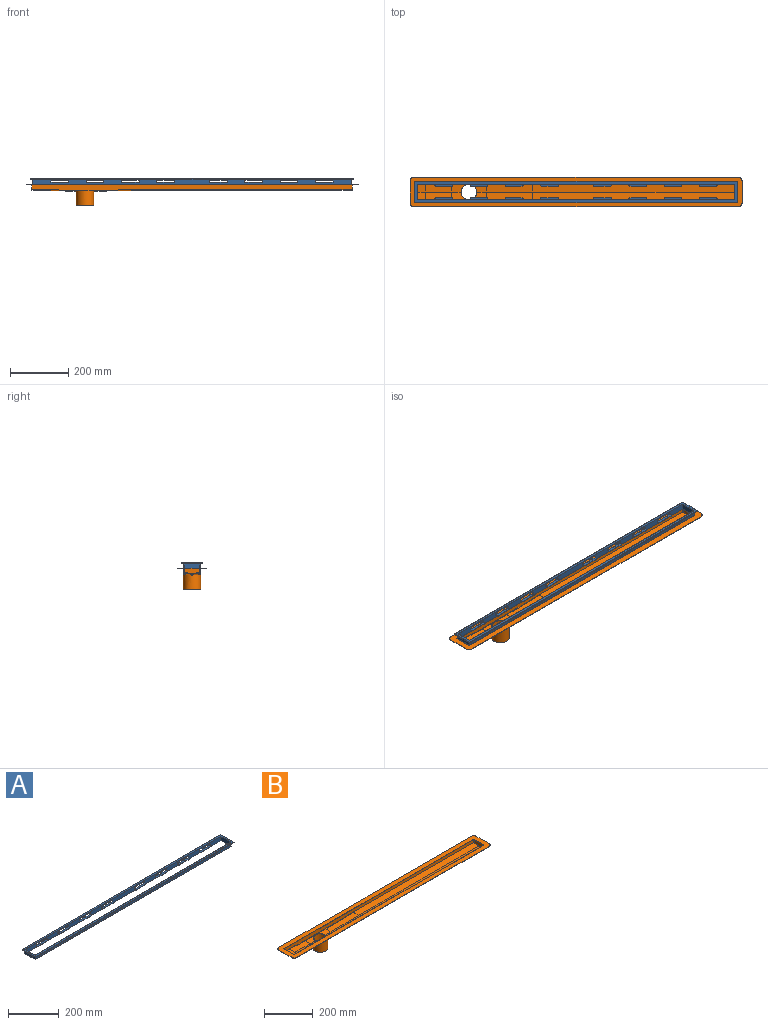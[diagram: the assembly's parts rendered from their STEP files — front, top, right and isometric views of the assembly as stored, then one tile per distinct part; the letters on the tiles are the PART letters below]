
ASSEMBLY  parts=2 mates=1
PART A: 212 faces, bbox 1112.8x73x20.6 mm
  f0: plane 1093.79x20.64mm, normal (0,1,0), area 17992.5mm2, adj f6,f7,f9,f12,f13,f17,f19,f23
  f1: plane 1096.96x19.05mm, normal (0,-1,0), area 17088.3mm2, adj f2,f6,f10,f18,f25,f32,f39,f40
  f2: plane 1109.66x69.85mm, normal (0,0,-1), area 14818.5mm2, adj f1,f5,f10,f11,f61,f63,f114,f115
  f3: plane 1112.84x3.18mm, normal (0,-1,0), area 3533.3mm2, adj f4,f7,f8,f112
  f4: plane 1112.84x73.03mm, normal (0,0,-1), area 3755mm2, adj f3,f5,f8,f11,f62,f63,f112,f115
  f5: plane 1109.66x1.59mm, normal (0,1,0), area 1761.6mm2, adj f2,f4,f11,f115
  f6: plane 1096.96x57.15mm, normal (0,0,-1), area 3654.2mm2, adj f0,f1,f9,f10,f60,f61,f113,f114
  f7: plane 1112.84x73.03mm, normal (0,0,1), area 22227.8mm2, adj f0,f3,f8,f9,f60,f62,f112,f113
  f8: plane 73.03x3.18mm, normal (1,0,0), area 231.9mm2, adj f3,f4,f7,f62
  f9: plane 53.98x20.64mm, normal (-1,0,0), area 1113.9mm2, adj f0,f6,f7,f60
  f10: plane 57.15x19.05mm, normal (1,0,0), area 1088.7mm2, adj f1,f2,f6,f61
  f11: plane 69.85x1.59mm, normal (-1,0,0), area 110.9mm2, adj f2,f4,f5,f63
  f12: plane 4.13x1.59mm, normal (-1,0,0), area 6.6mm2, adj f0,f16,f17,f18
  f13: plane 4.13x1.59mm, normal (1,0,0), area 6.6mm2, adj f0,f14,f17,f18
  f14: cylinder r=3.81mm len=3.81mm, axis (0,0,1), area 9.5mm2, adj f13,f15,f17,f18
  f15: plane 53.15x1.59mm, normal (0,1,0), area 84.4mm2, adj f14,f16,f17,f18
  f16: cylinder r=3.81mm len=3.81mm, axis (0,0,1), area 9.5mm2, adj f12,f15,f17,f18
  f17: plane 60.77x7.94mm, normal (0,0,-1), area 476.1mm2, adj f0,f12,f13,f14,f15,f16
  f18: plane 60.77x9.53mm, normal (0,0,1), area 572.6mm2, adj f1,f12,f13,f14,f15,f16,f40,f44
  f19: plane 4.13x1.59mm, normal (1,0,0), area 6.6mm2, adj f0,f20,f24,f25
  f20: cylinder r=3.81mm len=3.81mm, axis (0,0,1), area 9.5mm2, adj f19,f21,f24,f25
  f21: plane 53.15x1.59mm, normal (0,1,0), area 84.4mm2, adj f20,f22,f24,f25
  f22: cylinder r=3.81mm len=3.81mm, axis (0,0,1), area 9.5mm2, adj f21,f23,f24,f25
  f23: plane 4.13x1.59mm, normal (-1,0,0), area 6.6mm2, adj f0,f22,f24,f25
  f24: plane 60.77x7.94mm, normal (0,0,-1), area 476.1mm2, adj f0,f19,f20,f21,f22,f23
  f25: plane 60.77x9.53mm, normal (0,0,1), area 572.6mm2, adj f1,f19,f20,f21,f22,f23,f45,f49
  f26: plane 4.13x1.59mm, normal (1,0,0), area 6.6mm2, adj f0,f27,f31,f32
  f27: cylinder r=3.81mm len=3.81mm, axis (0,0,1), area 9.5mm2, adj f26,f28,f31,f32
  f28: plane 53.15x1.59mm, normal (0,1,0), area 84.4mm2, adj f27,f29,f31,f32
  f29: cylinder r=3.81mm len=3.81mm, axis (0,0,1), area 9.5mm2, adj f28,f30,f31,f32
  f30: plane 4.13x1.59mm, normal (-1,0,0), area 6.6mm2, adj f0,f29,f31,f32
  f31: plane 60.77x7.94mm, normal (0,0,-1), area 476.1mm2, adj f0,f26,f27,f28,f29,f30
  f32: plane 60.77x9.53mm, normal (0,0,1), area 572.6mm2, adj f1,f26,f27,f28,f29,f30,f50,f54
  f33: plane 4.13x1.59mm, normal (1,0,0), area 6.6mm2, adj f0,f34,f38,f39
  f34: cylinder r=3.81mm len=3.81mm, axis (0,0,1), area 9.5mm2, adj f33,f35,f38,f39
  f35: plane 53.15x1.59mm, normal (0,1,0), area 84.4mm2, adj f34,f36,f38,f39
  f36: cylinder r=3.81mm len=3.81mm, axis (0,0,1), area 9.5mm2, adj f35,f37,f38,f39
  f37: plane 4.13x1.59mm, normal (-1,0,0), area 6.6mm2, adj f0,f36,f38,f39
  f38: plane 60.77x7.94mm, normal (0,0,-1), area 476.1mm2, adj f0,f33,f34,f35,f36,f37
  f39: plane 60.77x9.53mm, normal (0,0,1), area 572.6mm2, adj f1,f33,f34,f35,f36,f37,f56,f57
  f40: plane 4.13x1.59mm, normal (1,0,0), area 6.6mm2, adj f0,f1,f18,f41
  f41: cylinder r=3.81mm len=3.81mm, axis (0,1,0), area 9.5mm2, adj f0,f1,f40,f42
  f42: plane 53.15x1.59mm, normal (0,0,-1), area 84.4mm2, adj f0,f1,f41,f43
  f43: cylinder r=3.81mm len=3.81mm, axis (0,1,0), area 9.5mm2, adj f0,f1,f42,f44
  f44: plane 4.13x1.59mm, normal (-1,0,0), area 6.6mm2, adj f0,f1,f18,f43
  f45: plane 4.13x1.59mm, normal (1,0,0), area 6.6mm2, adj f0,f1,f25,f46
  f46: cylinder r=3.81mm len=3.81mm, axis (0,1,0), area 9.5mm2, adj f0,f1,f45,f47
  f47: plane 53.15x1.59mm, normal (0,0,-1), area 84.4mm2, adj f0,f1,f46,f48
  f48: cylinder r=3.81mm len=3.81mm, axis (0,1,0), area 9.5mm2, adj f0,f1,f47,f49
  f49: plane 4.13x1.59mm, normal (-1,0,0), area 6.6mm2, adj f0,f1,f25,f48
  f50: plane 4.13x1.59mm, normal (1,0,0), area 6.6mm2, adj f0,f1,f32,f51
  f51: cylinder r=3.81mm len=3.81mm, axis (0,1,0), area 9.5mm2, adj f0,f1,f50,f52
  f52: plane 53.15x1.59mm, normal (0,0,-1), area 84.4mm2, adj f0,f1,f51,f53
  f53: cylinder r=3.81mm len=3.81mm, axis (0,1,0), area 9.5mm2, adj f0,f1,f52,f54
  f54: plane 4.13x1.59mm, normal (-1,0,0), area 6.6mm2, adj f0,f1,f32,f53
  f55: cylinder r=3.81mm len=3.81mm, axis (0,1,0), area 9.5mm2, adj f0,f1,f56,f59
  f56: plane 4.13x1.59mm, normal (-1,0,0), area 6.6mm2, adj f0,f1,f39,f55
  f57: plane 4.13x1.59mm, normal (1,0,0), area 6.6mm2, adj f0,f1,f39,f58
  f58: cylinder r=3.81mm len=3.81mm, axis (0,1,0), area 9.5mm2, adj f0,f1,f57,f59
  f59: plane 53.15x1.59mm, normal (0,0,-1), area 84.4mm2, adj f0,f1,f55,f58
  f60: plane 1093.79x20.64mm, normal (0,-1,0), area 17992.5mm2, adj f6,f7,f9,f64,f65,f69,f71,f75
  f61: plane 1096.96x19.05mm, normal (0,1,0), area 17088.3mm2, adj f2,f6,f10,f70,f77,f84,f91,f92
  f62: plane 1112.84x3.18mm, normal (0,1,0), area 3533.3mm2, adj f4,f7,f8,f112
  f63: plane 1109.66x1.59mm, normal (0,-1,0), area 1761.6mm2, adj f2,f4,f11,f115
  f64: plane 4.13x1.59mm, normal (-1,0,0), area 6.6mm2, adj f60,f68,f69,f70
  f65: plane 4.13x1.59mm, normal (1,0,0), area 6.6mm2, adj f60,f66,f69,f70
  f66: cylinder r=3.81mm len=3.81mm, axis (0,0,1), area 9.5mm2, adj f65,f67,f69,f70
  f67: plane 53.15x1.59mm, normal (0,-1,0), area 84.4mm2, adj f66,f68,f69,f70
  f68: cylinder r=3.81mm len=3.81mm, axis (0,0,1), area 9.5mm2, adj f64,f67,f69,f70
  f69: plane 60.77x7.94mm, normal (0,0,-1), area 476.1mm2, adj f60,f64,f65,f66,f67,f68
  f70: plane 60.77x9.53mm, normal (0,0,1), area 572.6mm2, adj f61,f64,f65,f66,f67,f68,f92,f96
  f71: plane 4.13x1.59mm, normal (1,0,0), area 6.6mm2, adj f60,f72,f76,f77
  f72: cylinder r=3.81mm len=3.81mm, axis (0,0,1), area 9.5mm2, adj f71,f73,f76,f77
  f73: plane 53.15x1.59mm, normal (0,-1,0), area 84.4mm2, adj f72,f74,f76,f77
  f74: cylinder r=3.81mm len=3.81mm, axis (0,0,1), area 9.5mm2, adj f73,f75,f76,f77
  f75: plane 4.13x1.59mm, normal (-1,0,0), area 6.6mm2, adj f60,f74,f76,f77
  f76: plane 60.77x7.94mm, normal (0,0,-1), area 476.1mm2, adj f60,f71,f72,f73,f74,f75
  f77: plane 60.77x9.53mm, normal (0,0,1), area 572.6mm2, adj f61,f71,f72,f73,f74,f75,f97,f101
  f78: plane 4.13x1.59mm, normal (1,0,0), area 6.6mm2, adj f60,f79,f83,f84
  f79: cylinder r=3.81mm len=3.81mm, axis (0,0,1), area 9.5mm2, adj f78,f80,f83,f84
  f80: plane 53.15x1.59mm, normal (0,-1,0), area 84.4mm2, adj f79,f81,f83,f84
  f81: cylinder r=3.81mm len=3.81mm, axis (0,0,1), area 9.5mm2, adj f80,f82,f83,f84
  f82: plane 4.13x1.59mm, normal (-1,0,0), area 6.6mm2, adj f60,f81,f83,f84
  f83: plane 60.77x7.94mm, normal (0,0,-1), area 476.1mm2, adj f60,f78,f79,f80,f81,f82
  f84: plane 60.77x9.53mm, normal (0,0,1), area 572.6mm2, adj f61,f78,f79,f80,f81,f82,f102,f106
  f85: plane 4.13x1.59mm, normal (1,0,0), area 6.6mm2, adj f60,f86,f90,f91
  f86: cylinder r=3.81mm len=3.81mm, axis (0,0,1), area 9.5mm2, adj f85,f87,f90,f91
  f87: plane 53.15x1.59mm, normal (0,-1,0), area 84.4mm2, adj f86,f88,f90,f91
  f88: cylinder r=3.81mm len=3.81mm, axis (0,0,1), area 9.5mm2, adj f87,f89,f90,f91
  f89: plane 4.13x1.59mm, normal (-1,0,0), area 6.6mm2, adj f60,f88,f90,f91
  f90: plane 60.77x7.94mm, normal (0,0,-1), area 476.1mm2, adj f60,f85,f86,f87,f88,f89
  f91: plane 60.77x9.53mm, normal (0,0,1), area 572.6mm2, adj f61,f85,f86,f87,f88,f89,f108,f109
  f92: plane 4.13x1.59mm, normal (1,0,0), area 6.6mm2, adj f60,f61,f70,f93
  f93: cylinder r=3.81mm len=3.81mm, axis (0,-1,0), area 9.5mm2, adj f60,f61,f92,f94
  f94: plane 53.15x1.59mm, normal (0,0,-1), area 84.4mm2, adj f60,f61,f93,f95
  f95: cylinder r=3.81mm len=3.81mm, axis (0,-1,0), area 9.5mm2, adj f60,f61,f94,f96
  f96: plane 4.13x1.59mm, normal (-1,0,0), area 6.6mm2, adj f60,f61,f70,f95
  f97: plane 4.13x1.59mm, normal (1,0,0), area 6.6mm2, adj f60,f61,f77,f98
  f98: cylinder r=3.81mm len=3.81mm, axis (0,-1,0), area 9.5mm2, adj f60,f61,f97,f99
  f99: plane 53.15x1.59mm, normal (0,0,-1), area 84.4mm2, adj f60,f61,f98,f100
  f100: cylinder r=3.81mm len=3.81mm, axis (0,-1,0), area 9.5mm2, adj f60,f61,f99,f101
  f101: plane 4.13x1.59mm, normal (-1,0,0), area 6.6mm2, adj f60,f61,f77,f100
  f102: plane 4.13x1.59mm, normal (1,0,0), area 6.6mm2, adj f60,f61,f84,f103
  f103: cylinder r=3.81mm len=3.81mm, axis (0,-1,0), area 9.5mm2, adj f60,f61,f102,f104
  f104: plane 53.15x1.59mm, normal (0,0,-1), area 84.4mm2, adj f60,f61,f103,f105
  f105: cylinder r=3.81mm len=3.81mm, axis (0,-1,0), area 9.5mm2, adj f60,f61,f104,f106
  f106: plane 4.13x1.59mm, normal (-1,0,0), area 6.6mm2, adj f60,f61,f84,f105
  f107: cylinder r=3.81mm len=3.81mm, axis (0,-1,0), area 9.5mm2, adj f60,f61,f108,f111
  f108: plane 4.13x1.59mm, normal (-1,0,0), area 6.6mm2, adj f60,f61,f91,f107
  f109: plane 4.13x1.59mm, normal (1,0,0), area 6.6mm2, adj f60,f61,f91,f110
  f110: cylinder r=3.81mm len=3.81mm, axis (0,-1,0), area 9.5mm2, adj f60,f61,f109,f111
  f111: plane 53.15x1.59mm, normal (0,0,-1), area 84.4mm2, adj f60,f61,f107,f110
  f112: plane 73.03x3.18mm, normal (-1,0,0), area 231.9mm2, adj f3,f4,f7,f62
  f113: plane 53.98x20.64mm, normal (1,0,0), area 1113.9mm2, adj f0,f6,f7,f60
  f114: plane 57.15x19.05mm, normal (-1,0,0), area 1088.7mm2, adj f1,f2,f6,f61
  f115: plane 69.85x1.59mm, normal (1,0,0), area 110.9mm2, adj f2,f4,f5,f63
  f116: plane 4.13x1.59mm, normal (1,0,0), area 6.6mm2, adj f0,f120,f121,f122
  f117: plane 4.13x1.59mm, normal (-1,0,0), area 6.6mm2, adj f0,f118,f121,f122
  f118: cylinder r=3.81mm len=3.81mm, axis (0,0,1), area 9.5mm2, adj f117,f119,f121,f122
  f119: plane 53.15x1.59mm, normal (0,1,0), area 84.4mm2, adj f118,f120,f121,f122
  f120: cylinder r=3.81mm len=3.81mm, axis (0,0,1), area 9.5mm2, adj f116,f119,f121,f122
  f121: plane 60.77x7.94mm, normal (0,0,-1), area 476.1mm2, adj f0,f116,f117,f118,f119,f120
  f122: plane 60.77x9.53mm, normal (0,0,1), area 572.6mm2, adj f1,f116,f117,f118,f119,f120,f144,f148
  f123: plane 4.13x1.59mm, normal (-1,0,0), area 6.6mm2, adj f0,f124,f128,f129
  f124: cylinder r=3.81mm len=3.81mm, axis (0,0,1), area 9.5mm2, adj f123,f125,f128,f129
  f125: plane 53.15x1.59mm, normal (0,1,0), area 84.4mm2, adj f124,f126,f128,f129
  f126: cylinder r=3.81mm len=3.81mm, axis (0,0,1), area 9.5mm2, adj f125,f127,f128,f129
  f127: plane 4.13x1.59mm, normal (1,0,0), area 6.6mm2, adj f0,f126,f128,f129
  f128: plane 60.77x7.94mm, normal (0,0,-1), area 476.1mm2, adj f0,f123,f124,f125,f126,f127
  f129: plane 60.77x9.53mm, normal (0,0,1), area 572.6mm2, adj f1,f123,f124,f125,f126,f127,f149,f153
  f130: plane 4.13x1.59mm, normal (-1,0,0), area 6.6mm2, adj f0,f131,f135,f136
  f131: cylinder r=3.81mm len=3.81mm, axis (0,0,1), area 9.5mm2, adj f130,f132,f135,f136
  f132: plane 53.15x1.59mm, normal (0,1,0), area 84.4mm2, adj f131,f133,f135,f136
  f133: cylinder r=3.81mm len=3.81mm, axis (0,0,1), area 9.5mm2, adj f132,f134,f135,f136
  f134: plane 4.13x1.59mm, normal (1,0,0), area 6.6mm2, adj f0,f133,f135,f136
  f135: plane 60.77x7.94mm, normal (0,0,-1), area 476.1mm2, adj f0,f130,f131,f132,f133,f134
  f136: plane 60.77x9.53mm, normal (0,0,1), area 572.6mm2, adj f1,f130,f131,f132,f133,f134,f154,f158
  f137: plane 4.13x1.59mm, normal (-1,0,0), area 6.6mm2, adj f0,f138,f142,f143
  f138: cylinder r=3.81mm len=3.81mm, axis (0,0,1), area 9.5mm2, adj f137,f139,f142,f143
  f139: plane 53.15x1.59mm, normal (0,1,0), area 84.4mm2, adj f138,f140,f142,f143
  f140: cylinder r=3.81mm len=3.81mm, axis (0,0,1), area 9.5mm2, adj f139,f141,f142,f143
  f141: plane 4.13x1.59mm, normal (1,0,0), area 6.6mm2, adj f0,f140,f142,f143
  f142: plane 60.77x7.94mm, normal (0,0,-1), area 476.1mm2, adj f0,f137,f138,f139,f140,f141
  f143: plane 60.77x9.53mm, normal (0,0,1), area 572.6mm2, adj f1,f137,f138,f139,f140,f141,f160,f161
  f144: plane 4.13x1.59mm, normal (-1,0,0), area 6.6mm2, adj f0,f1,f122,f145
  f145: cylinder r=3.81mm len=3.81mm, axis (0,1,0), area 9.5mm2, adj f0,f1,f144,f146
  f146: plane 53.15x1.59mm, normal (0,0,-1), area 84.4mm2, adj f0,f1,f145,f147
  f147: cylinder r=3.81mm len=3.81mm, axis (0,1,0), area 9.5mm2, adj f0,f1,f146,f148
  f148: plane 4.13x1.59mm, normal (1,0,0), area 6.6mm2, adj f0,f1,f122,f147
  f149: plane 4.13x1.59mm, normal (-1,0,0), area 6.6mm2, adj f0,f1,f129,f150
  f150: cylinder r=3.81mm len=3.81mm, axis (0,1,0), area 9.5mm2, adj f0,f1,f149,f151
  f151: plane 53.15x1.59mm, normal (0,0,-1), area 84.4mm2, adj f0,f1,f150,f152
  f152: cylinder r=3.81mm len=3.81mm, axis (0,1,0), area 9.5mm2, adj f0,f1,f151,f153
  f153: plane 4.13x1.59mm, normal (1,0,0), area 6.6mm2, adj f0,f1,f129,f152
  f154: plane 4.13x1.59mm, normal (-1,0,0), area 6.6mm2, adj f0,f1,f136,f155
  f155: cylinder r=3.81mm len=3.81mm, axis (0,1,0), area 9.5mm2, adj f0,f1,f154,f156
  f156: plane 53.15x1.59mm, normal (0,0,-1), area 84.4mm2, adj f0,f1,f155,f157
  f157: cylinder r=3.81mm len=3.81mm, axis (0,1,0), area 9.5mm2, adj f0,f1,f156,f158
  f158: plane 4.13x1.59mm, normal (1,0,0), area 6.6mm2, adj f0,f1,f136,f157
  f159: cylinder r=3.81mm len=3.81mm, axis (0,1,0), area 9.5mm2, adj f0,f1,f160,f163
  f160: plane 4.13x1.59mm, normal (1,0,0), area 6.6mm2, adj f0,f1,f143,f159
  f161: plane 4.13x1.59mm, normal (-1,0,0), area 6.6mm2, adj f0,f1,f143,f162
  f162: cylinder r=3.81mm len=3.81mm, axis (0,1,0), area 9.5mm2, adj f0,f1,f161,f163
  f163: plane 53.15x1.59mm, normal (0,0,-1), area 84.4mm2, adj f0,f1,f159,f162
  f164: plane 4.13x1.59mm, normal (1,0,0), area 6.6mm2, adj f60,f168,f169,f170
  f165: plane 4.13x1.59mm, normal (-1,0,0), area 6.6mm2, adj f60,f166,f169,f170
  f166: cylinder r=3.81mm len=3.81mm, axis (0,0,1), area 9.5mm2, adj f165,f167,f169,f170
  f167: plane 53.15x1.59mm, normal (0,-1,0), area 84.4mm2, adj f166,f168,f169,f170
  f168: cylinder r=3.81mm len=3.81mm, axis (0,0,1), area 9.5mm2, adj f164,f167,f169,f170
  f169: plane 60.77x7.94mm, normal (0,0,-1), area 476.1mm2, adj f60,f164,f165,f166,f167,f168
  f170: plane 60.77x9.53mm, normal (0,0,1), area 572.6mm2, adj f61,f164,f165,f166,f167,f168,f192,f196
  f171: plane 4.13x1.59mm, normal (-1,0,0), area 6.6mm2, adj f60,f172,f176,f177
  f172: cylinder r=3.81mm len=3.81mm, axis (0,0,1), area 9.5mm2, adj f171,f173,f176,f177
  f173: plane 53.15x1.59mm, normal (0,-1,0), area 84.4mm2, adj f172,f174,f176,f177
  f174: cylinder r=3.81mm len=3.81mm, axis (0,0,1), area 9.5mm2, adj f173,f175,f176,f177
  f175: plane 4.13x1.59mm, normal (1,0,0), area 6.6mm2, adj f60,f174,f176,f177
  f176: plane 60.77x7.94mm, normal (0,0,-1), area 476.1mm2, adj f60,f171,f172,f173,f174,f175
  f177: plane 60.77x9.53mm, normal (0,0,1), area 572.6mm2, adj f61,f171,f172,f173,f174,f175,f197,f201
  f178: plane 4.13x1.59mm, normal (-1,0,0), area 6.6mm2, adj f60,f179,f183,f184
  f179: cylinder r=3.81mm len=3.81mm, axis (0,0,1), area 9.5mm2, adj f178,f180,f183,f184
  f180: plane 53.15x1.59mm, normal (0,-1,0), area 84.4mm2, adj f179,f181,f183,f184
  f181: cylinder r=3.81mm len=3.81mm, axis (0,0,1), area 9.5mm2, adj f180,f182,f183,f184
  f182: plane 4.13x1.59mm, normal (1,0,0), area 6.6mm2, adj f60,f181,f183,f184
  f183: plane 60.77x7.94mm, normal (0,0,-1), area 476.1mm2, adj f60,f178,f179,f180,f181,f182
  f184: plane 60.77x9.53mm, normal (0,0,1), area 572.6mm2, adj f61,f178,f179,f180,f181,f182,f202,f206
  f185: plane 4.13x1.59mm, normal (-1,0,0), area 6.6mm2, adj f60,f186,f190,f191
  f186: cylinder r=3.81mm len=3.81mm, axis (0,0,1), area 9.5mm2, adj f185,f187,f190,f191
  f187: plane 53.15x1.59mm, normal (0,-1,0), area 84.4mm2, adj f186,f188,f190,f191
  f188: cylinder r=3.81mm len=3.81mm, axis (0,0,1), area 9.5mm2, adj f187,f189,f190,f191
  f189: plane 4.13x1.59mm, normal (1,0,0), area 6.6mm2, adj f60,f188,f190,f191
  f190: plane 60.77x7.94mm, normal (0,0,-1), area 476.1mm2, adj f60,f185,f186,f187,f188,f189
  f191: plane 60.77x9.53mm, normal (0,0,1), area 572.6mm2, adj f61,f185,f186,f187,f188,f189,f208,f209
  f192: plane 4.13x1.59mm, normal (-1,0,0), area 6.6mm2, adj f60,f61,f170,f193
  f193: cylinder r=3.81mm len=3.81mm, axis (0,-1,0), area 9.5mm2, adj f60,f61,f192,f194
  f194: plane 53.15x1.59mm, normal (0,0,-1), area 84.4mm2, adj f60,f61,f193,f195
  f195: cylinder r=3.81mm len=3.81mm, axis (0,-1,0), area 9.5mm2, adj f60,f61,f194,f196
  f196: plane 4.13x1.59mm, normal (1,0,0), area 6.6mm2, adj f60,f61,f170,f195
  f197: plane 4.13x1.59mm, normal (-1,0,0), area 6.6mm2, adj f60,f61,f177,f198
  f198: cylinder r=3.81mm len=3.81mm, axis (0,-1,0), area 9.5mm2, adj f60,f61,f197,f199
  f199: plane 53.15x1.59mm, normal (0,0,-1), area 84.4mm2, adj f60,f61,f198,f200
  f200: cylinder r=3.81mm len=3.81mm, axis (0,-1,0), area 9.5mm2, adj f60,f61,f199,f201
  f201: plane 4.13x1.59mm, normal (1,0,0), area 6.6mm2, adj f60,f61,f177,f200
  f202: plane 4.13x1.59mm, normal (-1,0,0), area 6.6mm2, adj f60,f61,f184,f203
  f203: cylinder r=3.81mm len=3.81mm, axis (0,-1,0), area 9.5mm2, adj f60,f61,f202,f204
  f204: plane 53.15x1.59mm, normal (0,0,-1), area 84.4mm2, adj f60,f61,f203,f205
  f205: cylinder r=3.81mm len=3.81mm, axis (0,-1,0), area 9.5mm2, adj f60,f61,f204,f206
  f206: plane 4.13x1.59mm, normal (1,0,0), area 6.6mm2, adj f60,f61,f184,f205
  f207: cylinder r=3.81mm len=3.81mm, axis (0,-1,0), area 9.5mm2, adj f60,f61,f208,f211
  f208: plane 4.13x1.59mm, normal (1,0,0), area 6.6mm2, adj f60,f61,f191,f207
  f209: plane 4.13x1.59mm, normal (-1,0,0), area 6.6mm2, adj f60,f61,f191,f210
  f210: cylinder r=3.81mm len=3.81mm, axis (0,-1,0), area 9.5mm2, adj f60,f61,f209,f211
  f211: plane 53.15x1.59mm, normal (0,0,-1), area 84.4mm2, adj f60,f61,f207,f210
PART B: 65 faces, bbox 1144.6x101.6x73 mm
  f0: plane 59.53x30.16mm, normal (0,-0.09,-1), area 1085.2mm2, adj f3,f7,f12,f63
  f1: plane 59.53x30.16mm, normal (0,-0.09,-1), area 1085.2mm2, adj f2,f7,f10,f63
  f2: plane 59.53x30.16mm, normal (0,0.09,-1), area 1085.2mm2, adj f1,f38,f41,f63
  f3: plane 59.53x30.16mm, normal (0,0.09,-1), area 1085.2mm2, adj f0,f38,f43,f63
  f4: plane 1144.59x101.6mm, normal (0,0,1), area 53280.2mm2, adj f5,f9,f18,f19,f21,f23,f25,f29
  f5: plane 1119.19x1.59mm, normal (0,-1,0), area 1776.7mm2, adj f4,f6,f35,f36
  f6: plane 1144.59x101.6mm, normal (0,0,-1), area 49594.3mm2, adj f5,f7,f18,f19,f20,f22,f35,f36
  f7: plane 1103.31x19.59mm, normal (0,-1,0), area 18890.8mm2, adj f0,f1,f6,f10,f12,f14,f17,f20
  f8: plane 119.06x27.42mm, normal (0,0.09,1), area 2128.2mm2, adj f11,f13,f31,f39,f64
  f9: plane 1097.6x18.56mm, normal (0,1,0), area 17665.3mm2, adj f4,f25,f27,f28,f29,f31,f33,f34
  f10: plane 160.34x30.16mm, normal (0.02,-0.09,-1), area 4855.6mm2, adj f1,f7,f14,f41
  f11: plane 160.34x27.42mm, normal (-0.02,0.09,1), area 4413.4mm2, adj f8,f15,f28,f42
  f12: plane 91.28x30.16mm, normal (-0.03,-0.09,-1), area 2765.4mm2, adj f0,f7,f17,f43
  f13: plane 91.28x27.42mm, normal (0.03,0.09,1), area 2513.6mm2, adj f8,f16,f33,f44
  f14: plane 700.88x30.16mm, normal (0,-0.09,-1), area 21221.1mm2, adj f7,f10,f20,f45
  f15: plane 698.02x27.42mm, normal (0,0.09,1), area 19209.9mm2, adj f11,f24,f27,f46
  f16: plane 28.89x27.42mm, normal (0,0.09,1), area 795.1mm2, adj f13,f30,f34,f47
  f17: plane 31.75x30.16mm, normal (0,-0.09,-1), area 961.3mm2, adj f7,f12,f22,f48
  f18: plane 76.2x1.59mm, normal (1,0,0), area 121mm2, adj f4,f6,f36,f61
  f19: plane 76.2x1.59mm, normal (-1,0,0), area 121mm2, adj f4,f6,f35,f60
  f20: plane 60.33x19.06mm, normal (1,0,0), area 1070mm2, adj f6,f7,f14,f38,f45
  f21: plane 54.61x17.78mm, normal (-1,0,0), area 905.5mm2, adj f4,f24,f25,f49,f50
  f22: plane 60.33x19.06mm, normal (-1,0,0), area 1070mm2, adj f6,f7,f17,f38,f48
  f23: plane 54.61x17.78mm, normal (1,0,0), area 905.5mm2, adj f4,f29,f30,f54,f55
  f24: cylinder r=1.27mm len=27.53mm, axis (0,-1,0.09), area 54.8mm2, adj f15,f21,f26,f49
  f25: cylinder r=1.27mm len=15.39mm, axis (0,0,1), area 30.7mm2, adj f4,f9,f21,f26
  f26: sphere r=1.27mm, area 2.4mm2, adj f24,f25,f27
  f27: cylinder r=1.27mm len=698.04mm, axis (1,0,0), area 1315.1mm2, adj f9,f15,f26,f28
  f28: cylinder r=1.27mm len=160.38mm, axis (1,0,0.02), area 302.2mm2, adj f9,f11,f27,f31
  f29: cylinder r=1.27mm len=15.39mm, axis (0,0,1), area 30.7mm2, adj f4,f9,f23,f32
  f30: cylinder r=1.27mm len=27.53mm, axis (0,-1,0.09), area 54.8mm2, adj f16,f23,f32,f55
  f31: cylinder r=1.27mm len=119.06mm, axis (1,0,0), area 224.3mm2, adj f8,f9,f28,f33
  f32: sphere r=1.27mm, area 2.4mm2, adj f29,f30,f34
  f33: cylinder r=1.27mm len=91.35mm, axis (1,0,-0.03), area 172.1mm2, adj f9,f13,f31,f34
  f34: cylinder r=1.27mm len=28.91mm, axis (-1,0,0), area 54.5mm2, adj f9,f16,f32,f33
  f35: cylinder r=12.7mm len=12.7mm, axis (0,0,-1), area 31.7mm2, adj f4,f5,f6,f19
  f36: cylinder r=12.7mm len=12.7mm, axis (0,0,1), area 31.7mm2, adj f4,f5,f6,f18
  f37: plane 1119.19x1.59mm, normal (0,1,0), area 1776.7mm2, adj f4,f6,f60,f61
  f38: plane 1103.31x19.59mm, normal (0,1,0), area 18890.8mm2, adj f2,f3,f6,f20,f22,f41,f43,f45
  f39: plane 119.06x27.42mm, normal (0,-0.09,1), area 2128.2mm2, adj f8,f42,f44,f56,f64
  f40: plane 1097.6x18.56mm, normal (0,-1,0), area 17665.3mm2, adj f4,f50,f52,f53,f54,f56,f58,f59
  f41: plane 160.34x30.16mm, normal (0.02,0.09,-1), area 4855.6mm2, adj f2,f10,f38,f45
  f42: plane 160.34x27.42mm, normal (-0.02,-0.09,1), area 4413.4mm2, adj f11,f39,f46,f53
  f43: plane 91.28x30.16mm, normal (-0.03,0.09,-1), area 2765.4mm2, adj f3,f12,f38,f48
  f44: plane 91.28x27.42mm, normal (0.03,-0.09,1), area 2513.6mm2, adj f13,f39,f47,f58
  f45: plane 700.88x30.16mm, normal (0,0.09,-1), area 21221.1mm2, adj f14,f20,f38,f41
  f46: plane 698.02x27.42mm, normal (0,-0.09,1), area 19209.9mm2, adj f15,f42,f49,f52
  f47: plane 28.89x27.42mm, normal (0,-0.09,1), area 795.1mm2, adj f16,f44,f55,f59
  f48: plane 31.75x30.16mm, normal (0,0.09,-1), area 961.3mm2, adj f17,f22,f38,f43
  f49: cylinder r=1.27mm len=27.53mm, axis (0,1,0.09), area 54.8mm2, adj f21,f24,f46,f51
  f50: cylinder r=1.27mm len=15.39mm, axis (0,0,1), area 30.7mm2, adj f4,f21,f40,f51
  f51: sphere r=1.27mm, area 2.4mm2, adj f49,f50,f52
  f52: cylinder r=1.27mm len=698.04mm, axis (1,0,0), area 1315.1mm2, adj f40,f46,f51,f53
  f53: cylinder r=1.27mm len=160.38mm, axis (1,0,0.02), area 302.2mm2, adj f40,f42,f52,f56
  f54: cylinder r=1.27mm len=15.39mm, axis (0,0,1), area 30.7mm2, adj f4,f23,f40,f57
  f55: cylinder r=1.27mm len=27.53mm, axis (0,1,0.09), area 54.8mm2, adj f23,f30,f47,f57
  f56: cylinder r=1.27mm len=119.06mm, axis (1,0,0), area 224.3mm2, adj f39,f40,f53,f58
  f57: sphere r=1.27mm, area 2.4mm2, adj f54,f55,f59
  f58: cylinder r=1.27mm len=91.35mm, axis (1,0,-0.03), area 172.1mm2, adj f40,f44,f56,f59
  f59: cylinder r=1.27mm len=28.91mm, axis (-1,0,0), area 54.5mm2, adj f40,f47,f57,f58
  f60: cylinder r=12.7mm len=12.7mm, axis (0,0,-1), area 31.7mm2, adj f4,f6,f19,f37
  f61: cylinder r=12.7mm len=12.7mm, axis (0,0,1), area 31.7mm2, adj f4,f6,f18,f37
  f62: plane 60.33x60.33mm, normal (0,0,-1), area 570mm2, adj f63,f64
  f63: cylinder r=30.16mm len=60.33mm, axis (0,0,-1), area 9643.8mm2, adj f0,f1,f2,f3,f62
  f64: cylinder r=26.99mm len=53.98mm, axis (0,0,-1), area 8868.9mm2, adj f8,f39,f62
PLACE A t=(369.09,0,19.05)mm
PLACE B at identity fixed
MATE fastened A.f6 <-> B.f6  axis (0,0,-1) through (369.09,0,-1.59)mm
